# Revit family: BVN_BRF-V
name_source: partatom
category: Mechanical Equipment
units: mm (PartAtom-declared; Revit-internal decimal feet)

## family parameters
Cut with Voids When Loaded = No
Host = Face
Part Type = Normal
Room Calculation Point = No
Round Connector Dimension = Use Diameter
Shared = No

## types (7) — shared parameters
Default Elevation = 1219 mm
Description = Roof Fan
Frequency = 50 Hz
Manufacturer = Bahçıvan Elektrik Motor San. ve Tic. Ltd. Şti.
Material = <By Category>
Model = BRF-V
Protection Class = 44
URL = http://www.bahcivanmotor.com.tr
g = 10 mm  [stored 0.0328084 ft]

## per-type parameters (varying)
| type | A | Air Flow | B | C | Capacitor (mF) | Current | D | D' | F | G | Insulation Class | Power | QE | Sound Pressure Level dB(A) | Speed(d/d) | Voltage | Weight | h_Alt | h_Ust | t |
| BRF-V 225 | 350 mm  [stored 1.14829 ft] | 850.0 m³/h | 295 mm  [stored 0.967848 ft] | 190 mm | 6 | 1 A | 335 mm  [stored 1.09908 ft] | 285 mm  [stored 0.935039 ft] | 305 mm | 10 mm  [stored 0.0328084 ft] | B | 220 W | 146 mm  [stored 0.479003 ft] | 43 | 2650 | 230 V | 7.00 kg | 108 mm | 72 mm | 2 mm  [stored 0.00656168 ft] |
| BRF-V 315 | 552 mm  [stored 1.81102 ft] | 2200.0 m³/h | 450 mm  [stored 1.47638 ft] | 330 mm | 3 | 1 A | 505 mm  [stored 1.65682 ft] | 450 mm  [stored 1.47638 ft] | 475 mm  [stored 1.5584 ft] | 10 mm  [stored 0.0328084 ft] | F | 155 W | 185 mm  [stored 0.606955 ft] | 45 | 1650 | 230 V | 22.00 kg | 192 mm  [stored 0.629921 ft] | 128 mm  [stored 0.419948 ft] | 13 mm |
| BRF-V 355 | 745 mm | 3250.0 m³/h | 607 mm  [stored 1.99147 ft] | 385 mm  [stored 1.26312 ft] | 8 | 1 A | 595 mm  [stored 1.9521 ft] | 540 mm  [stored 1.77165 ft] | 565 mm  [stored 1.85367 ft] | 10 mm  [stored 0.0328084 ft] | F | 255 W | 234 mm  [stored 0.767717 ft] | 46 | 1600 | 230 V | 34.00 kg | 225 mm  [stored 0.738189 ft] | 150 mm  [stored 0.492126 ft] | 13 mm |
| BRF-V 400 | 745 mm | 4521.0 m³/h | 607 mm  [stored 1.99147 ft] | 385 mm  [stored 1.26312 ft] | 10 | 2 A | 595 mm  [stored 1.9521 ft] | 540 mm  [stored 1.77165 ft] | 565 mm  [stored 1.85367 ft] | 10 mm  [stored 0.0328084 ft] | F | 460 W | 270 mm  [stored 0.885827 ft] | 47 | 1560 | 230 V | 39.00 kg | 225 mm  [stored 0.738189 ft] | 150 mm  [stored 0.492126 ft] | 13 mm |
| BRF-V 450 | 900 mm | 6000.0 m³/h | 742 mm | 512 mm  [stored 1.67979 ft] | 10 | 3 A | 665 mm | 605 mm  [stored 1.98491 ft] | 635 mm | 10 mm  [stored 0.0328084 ft] | F | 630 W | 282 mm | 50 | 1550 | 230 V | 51.00 kg | 301 mm | 201 mm | 13 mm |
| BRF-V 500 | 900 mm | 7600.0 m³/h | 742 mm | 512 mm  [stored 1.67979 ft] | 0 | 2 A | 665 mm | 605 mm  [stored 1.98491 ft] | 635 mm | 12 mm  [stored 0.0393701 ft] | F | 960 W | 320 mm  [stored 1.04987 ft] | 52 | 1400 | 380 V | 60.00 kg | 300 mm | 200 mm  [stored 0.656168 ft] | 13 mm |
| BRF-V 560 | 1190 mm | 9600.0 m³/h | 955 mm | 595 mm  [stored 1.9521 ft] | 0 | 3 A | 946 mm | 850 mm | 916 mm | 12 mm  [stored 0.0393701 ft] | F | 1515 W | 360 mm  [stored 1.1811 ft] | 60 | 1250 | 380 V | 99.00 kg | 350 mm  [stored 1.14829 ft] | 233 mm | 13 mm |

note: [stored X ft] marks values corroborated as IEEE doubles in the binary element streams (Revit-internal decimal feet)

## geometry (parser evidence)
native form markers: Sweep x2
no freeform markers — native parametric forms only
